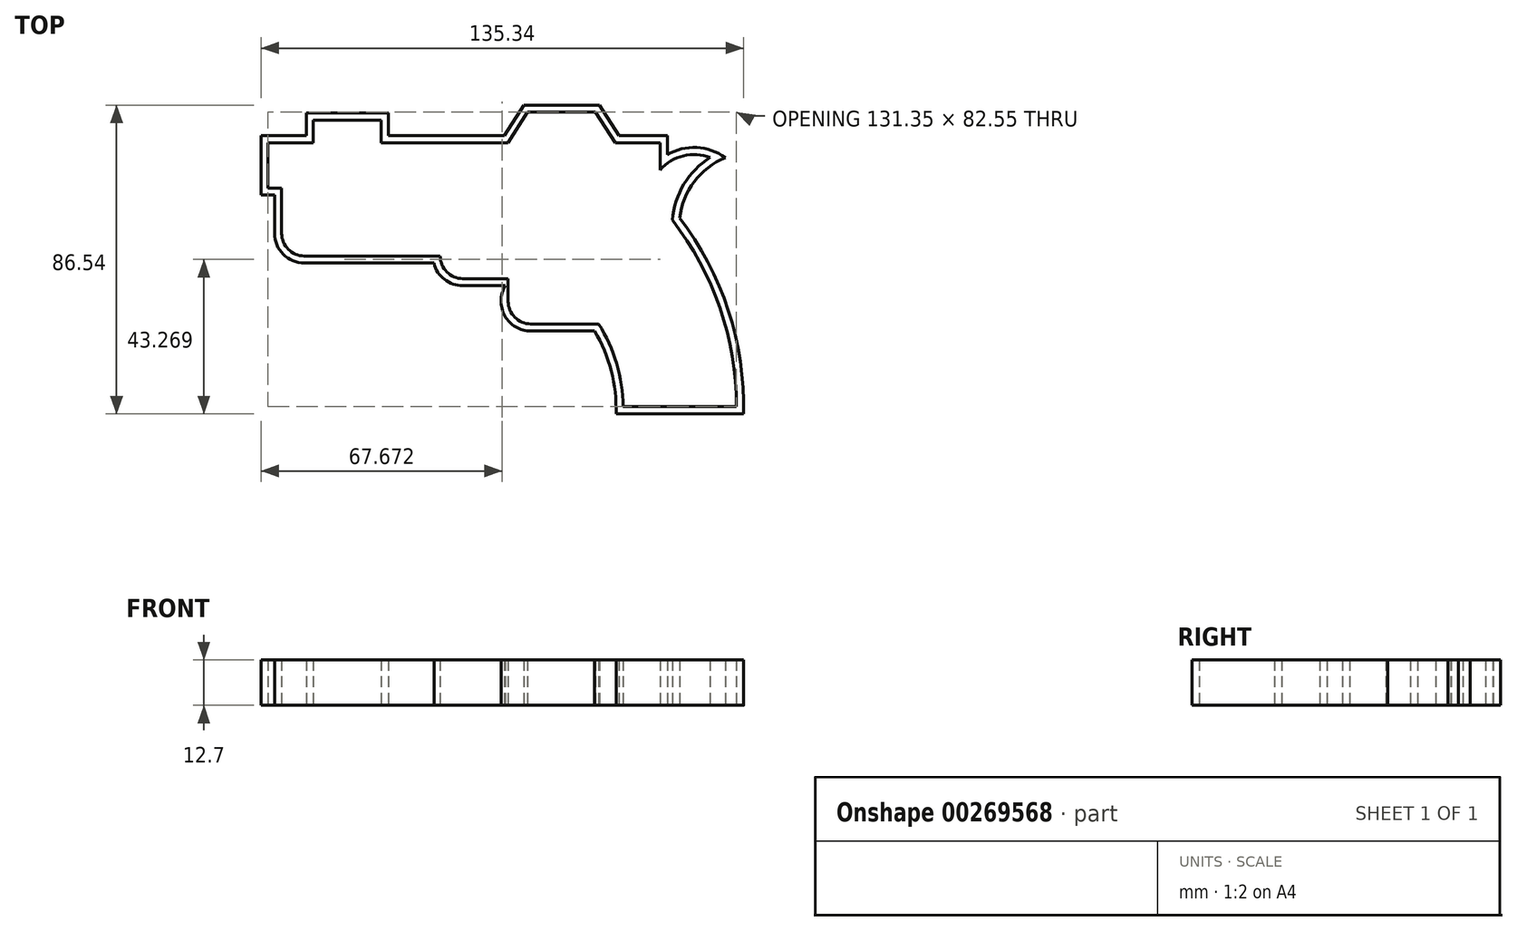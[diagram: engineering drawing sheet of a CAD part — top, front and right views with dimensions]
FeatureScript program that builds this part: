
annotation { "Feature Type Name" : "Feature", "Feature Type Description" : "" }
export const myFeature = defineFeature(function(context is Context, id is Id, definition is map)
    precondition{}
    {
        {
            var Q0;
            Q0=qCreatedBy(makeId("Top.planeOp"),FACE);
            var sketch = newSketch(context, id + "F0", { "sketchPlane" : qUnion([Q0])});
            skLineSegment(sketch, "E0", {"start": v(-14.2, -24.22) * mm, "end": v(17.54, -24.22) * mm});
            skArc(sketch, "E1", {"start": v(10.17, 45.63) * mm, "mid": v(2.6, 46.07) * mm, "end": v(-3.88, 42.15) * mm});
            skLineSegment(sketch, "E2", {"start": v(-3.88, 42.15) * mm, "end": v(-3.88, 49.77) * mm});
            skLineSegment(sketch, "E3", {"start": v(-3.88, 49.77) * mm, "end": v(-16.47, 49.77) * mm});
            skLineSegment(sketch, "E4", {"start": v(-16.47, 49.77) * mm, "end": v(-21.96, 58.32) * mm});
            skLineSegment(sketch, "E5", {"start": v(-21.96, 58.32) * mm, "end": v(-41, 58.32) * mm});
            skLineSegment(sketch, "E6", {"start": v(-41, 58.32) * mm, "end": v(-46.5, 49.77) * mm});
            skLineSegment(sketch, "E7", {"start": v(-46.5, 49.77) * mm, "end": v(-82.05, 49.77) * mm});
            skLineSegment(sketch, "E8", {"start": v(-82.05, 49.77) * mm, "end": v(-82.05, 56.12) * mm});
            skLineSegment(sketch, "E9", {"start": v(-82.05, 56.12) * mm, "end": v(-101.1, 56.12) * mm});
            skLineSegment(sketch, "E10", {"start": v(-101.1, 56.12) * mm, "end": v(-101.1, 49.77) * mm});
            skLineSegment(sketch, "E11", {"start": v(-101.1, 49.77) * mm, "end": v(-113.8, 49.77) * mm});
            skLineSegment(sketch, "E12", {"start": v(-113.8, 49.77) * mm, "end": v(-113.8, 37.07) * mm});
            skLineSegment(sketch, "E13", {"start": v(-113.8, 37.07) * mm, "end": v(-109.98, 37.07) * mm});
            skLineSegment(sketch, "E14", {"start": v(-109.98, 37.07) * mm, "end": v(-109.98, 24.37) * mm});
            skLineSegment(sketch, "E15", {"start": v(-103.63, 18.02) * mm, "end": v(-65.53, 18.02) * mm});
            skPoint(sketch, "E16.visualSharp", {"position": v(-109.98, 18.02) * mm});
            skArc(sketch, "E16.filletArc", {"start": v(-109.98, 24.37) * mm, "mid": v(-108.12, 19.88) * mm, "end": v(-103.63, 18.02) * mm});
            skLineSegment(sketch, "E17", {"start": v(-65.53, 18.02) * mm, "end": v(-65.53, 18.02) * mm});
            skLineSegment(sketch, "E18", {"start": v(-59.18, 11.67) * mm, "end": v(-46.48, 11.67) * mm});
            skPoint(sketch, "E19.visualSharp", {"position": v(-65.53, 11.67) * mm});
            skArc(sketch, "E19.filletArc", {"start": v(-65.53, 18.02) * mm, "mid": v(-63.67, 13.53) * mm, "end": v(-59.18, 11.67) * mm});
            skLineSegment(sketch, "E20", {"start": v(-46.48, 11.67) * mm, "end": v(-46.48, 5.32) * mm});
            skLineSegment(sketch, "E21", {"start": v(-40.13, -1.03) * mm, "end": v(-21.08, -1.03) * mm});
            skArc(sketch, "E22", {"start": v(-14.2, -24.22) * mm, "mid": v(-16.08, -12.16) * mm, "end": v(-21.08, -1.03) * mm});
            skPoint(sketch, "E23.visualSharp", {"position": v(-46.48, -1.03) * mm});
            skArc(sketch, "E23.filletArc", {"start": v(-46.48, 5.32) * mm, "mid": v(-44.62, 0.83) * mm, "end": v(-40.13, -1.03) * mm});
            skArc(sketch, "E24", {"start": v(17.54, -24.22) * mm, "mid": v(12.91, 3.45) * mm, "end": v(-0.48, 28.1) * mm});
            skArc(sketch, "E25", {"start": v(10.17, 45.63) * mm, "mid": v(2.8, 38.1) * mm, "end": v(-0.48, 28.1) * mm});
            skLineSegment(sketch, "E26.0", {"start": v(-103.1, 58.12) * mm, "end": v(-103.1, 51.77) * mm});
            skArc(sketch, "E26.1", {"start": v(-16.2, -26.22) * mm, "mid": v(-17.59, -14.2) * mm, "end": v(-22.2, -3.03) * mm});
            skLineSegment(sketch, "E26.2", {"start": v(-40.13, -3.03) * mm, "end": v(-22.2, -3.03) * mm});
            skArc(sketch, "E26.3", {"start": v(-47.25, 9.67) * mm, "mid": v(-47.41, 1.24) * mm, "end": v(-40.13, -3.03) * mm});
            skLineSegment(sketch, "E26.4", {"start": v(-59.18, 9.67) * mm, "end": v(-47.25, 9.67) * mm});
            skArc(sketch, "E26.5", {"start": v(-67.29, 16.02) * mm, "mid": v(-64.33, 11.45) * mm, "end": v(-59.18, 9.67) * mm});
            skLineSegment(sketch, "E26.6", {"start": v(-103.63, 16.02) * mm, "end": v(-67.29, 16.02) * mm});
            skLineSegment(sketch, "E26.7", {"start": v(-115.8, 51.77) * mm, "end": v(-115.8, 35.07) * mm});
            skLineSegment(sketch, "E26.8", {"start": v(-115.8, 35.07) * mm, "end": v(-111.98, 35.07) * mm});
            skLineSegment(sketch, "E26.9", {"start": v(-111.98, 35.07) * mm, "end": v(-111.98, 24.37) * mm});
            skArc(sketch, "E26.10", {"start": v(-111.98, 24.37) * mm, "mid": v(-109.53, 18.47) * mm, "end": v(-103.63, 16.02) * mm});
            skLineSegment(sketch, "E26.11", {"start": v(-16.2, -26.22) * mm, "end": v(19.52, -26.22) * mm});
            skLineSegment(sketch, "E26.12", {"start": v(-103.1, 51.77) * mm, "end": v(-115.8, 51.77) * mm});
            skArc(sketch, "E26.13", {"start": v(19.52, -26.22) * mm, "mid": v(15.25, 2.77) * mm, "end": v(1.59, 28.69) * mm});
            skArc(sketch, "E26.14", {"start": v(14.4, 45.59) * mm, "mid": v(5.73, 38.86) * mm, "end": v(1.59, 28.69) * mm});
            skArc(sketch, "E26.15", {"start": v(14.4, 45.59) * mm, "mid": v(6.38, 48.43) * mm, "end": v(-1.88, 46.37) * mm});
            skLineSegment(sketch, "E26.16", {"start": v(-1.88, 46.37) * mm, "end": v(-1.88, 51.77) * mm});
            skLineSegment(sketch, "E26.17", {"start": v(-1.88, 51.77) * mm, "end": v(-15.38, 51.77) * mm});
            skLineSegment(sketch, "E26.18", {"start": v(-15.38, 51.77) * mm, "end": v(-20.86, 60.32) * mm});
            skLineSegment(sketch, "E26.19", {"start": v(-20.86, 60.32) * mm, "end": v(-42.1, 60.32) * mm});
            skLineSegment(sketch, "E26.20", {"start": v(-42.1, 60.32) * mm, "end": v(-47.58, 51.77) * mm});
            skLineSegment(sketch, "E26.21", {"start": v(-47.58, 51.77) * mm, "end": v(-80.05, 51.77) * mm});
            skLineSegment(sketch, "E26.22", {"start": v(-80.05, 51.77) * mm, "end": v(-80.05, 58.12) * mm});
            skLineSegment(sketch, "E26.23", {"start": v(-80.05, 58.12) * mm, "end": v(-103.1, 58.12) * mm});
            skSolve(sketch);
        }
        {
            var Q0;
            Q0 = qSketchRegion(id + "F0", true);
            extrude(context, id + "F1", {"entities" : qUnion([Q0]), "depth" : 12.7 * mm});
        }
    });
